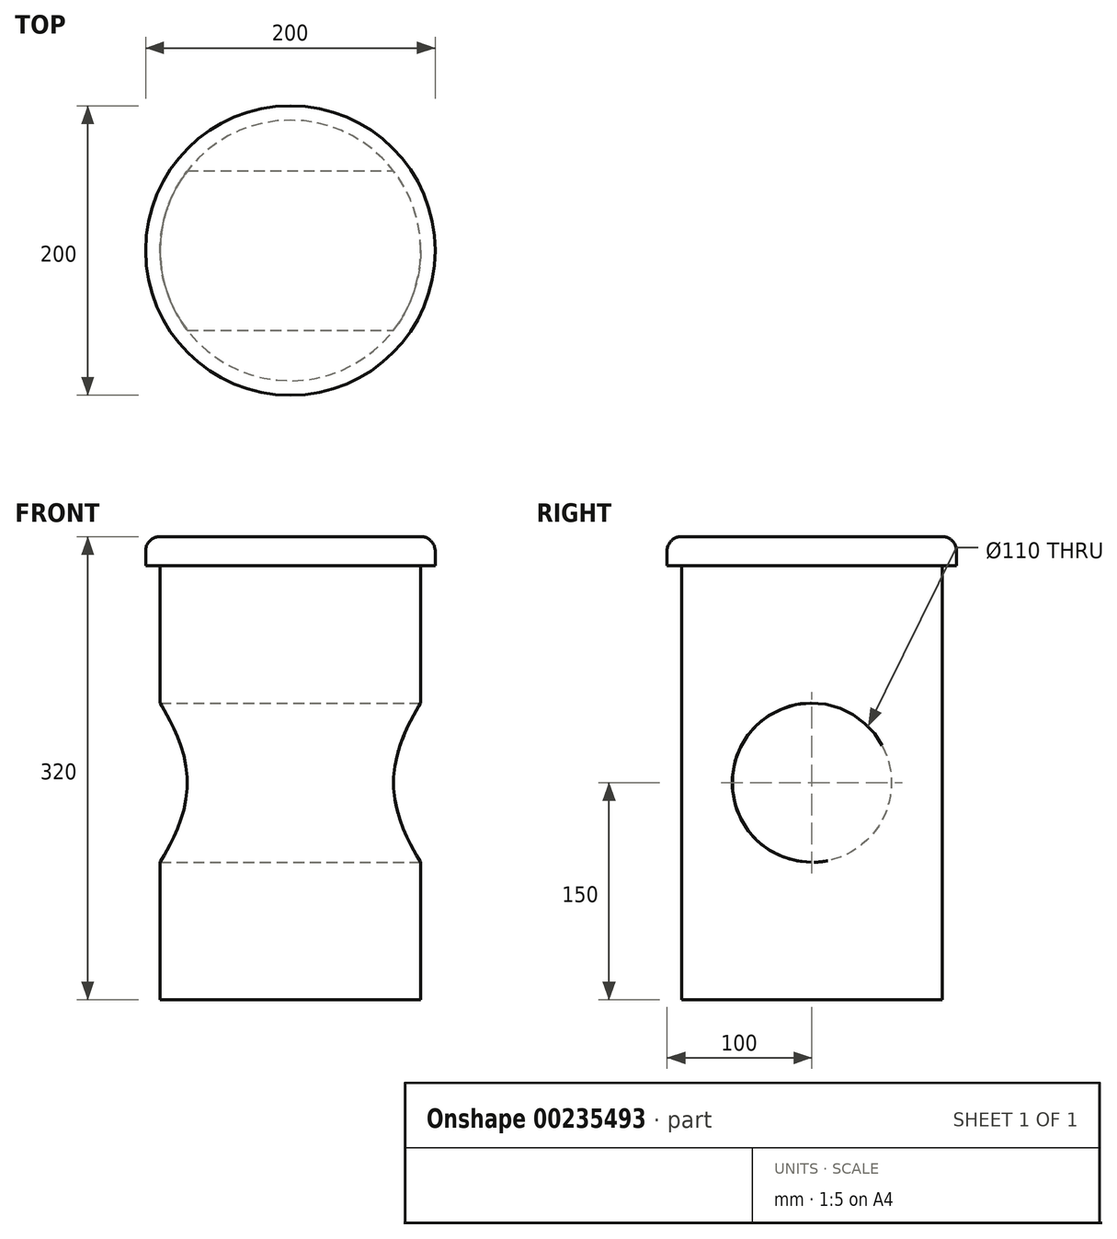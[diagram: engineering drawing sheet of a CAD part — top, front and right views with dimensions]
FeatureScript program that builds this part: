
annotation { "Feature Type Name" : "Feature", "Feature Type Description" : "" }
export const myFeature = defineFeature(function(context is Context, id is Id, definition is map)
    precondition{}
    {
        {
            var Q0;
            Q0=qCreatedBy(makeId("Top.planeOp"),FACE);
            var sketch = newSketch(context, id + "F0", { "sketchPlane" : qUnion([Q0])});
            skCircle(sketch, "E0", {"center": v(0, 0) * mm, "radius": 100 * mm});
            skCircle(sketch, "E1", {"center": v(0, 0) * mm, "radius": 90 * mm});
            skSolve(sketch);
        }
        {
            var Q0;
            Q0=makeQuery(id+"F0.imprint","IMPRINT",FACE,{"disambiguationData":[TD([[makeQuery(id+"F0.imprint","IMPRINT",EDGE,{"derivedFrom":sQuery(id+"F0.wireOp",EDGE,"E0")}),1.0]])]});
            extrude(context, id + "F1", {"entities" : qUnion([Q0]), "oppositeDirection" : true, "depth" : 20 * mm});
        }
        {
            var Q0;
            Q0=makeQuery(id+"F0.imprint","IMPRINT",FACE,{"disambiguationData":[TD([[makeQuery(id+"F0.imprint","IMPRINT",EDGE,{"derivedFrom":sQuery(id+"F0.wireOp",EDGE,"E1")}),1.0]])]});
            extrude(context, id + "F2", {"entities" : qUnion([Q0]), "operationType" : NewBodyOperationType.ADD, "oppositeDirection" : true, "depth" : 320 * mm});
        }
        {
            var Q0;
            Q0=makeQuery(id+"F1.opExtrude","CAP_EDGE",EDGE,{"disambiguationData":[OSD([sQuery(id+"F0.wireOp",EDGE,"E0")])],"isStart":true});
            fillet(context, id + "F3", {"entities" : qUnion([Q0]), "radius" : 10 * mm, "tangentPropagation" : true, "allowEdgeOverflow" : false});
        }
        {
            var Q0;
            Q0=qCreatedBy(makeId("Right.planeOp"),FACE);
            var sketch = newSketch(context, id + "F4", { "sketchPlane" : qUnion([Q0])});
            skLineSegment(sketch, "E2", {"start": v(0, 40.25) * mm, "end": v(0, -278.33) * mm, "construction": true});
            skLineSegment(sketch, "E3", {"start": v(-122.2, -170) * mm, "end": v(179.97, -170) * mm, "construction": true});
            skCircle(sketch, "E4", {"center": v(0, -170) * mm, "radius": 55 * mm});
            skSolve(sketch);
        }
        {
            var Q0;
            Q0 = qSketchRegion(id + "F4", true);
            extrude(context, id + "F5", {"entities" : qUnion([Q0]), "operationType" : NewBodyOperationType.REMOVE, "endBound" : BoundingType.SYMMETRIC, "oppositeDirection" : true, "depth" : 1000 * mm});
        }
    });
